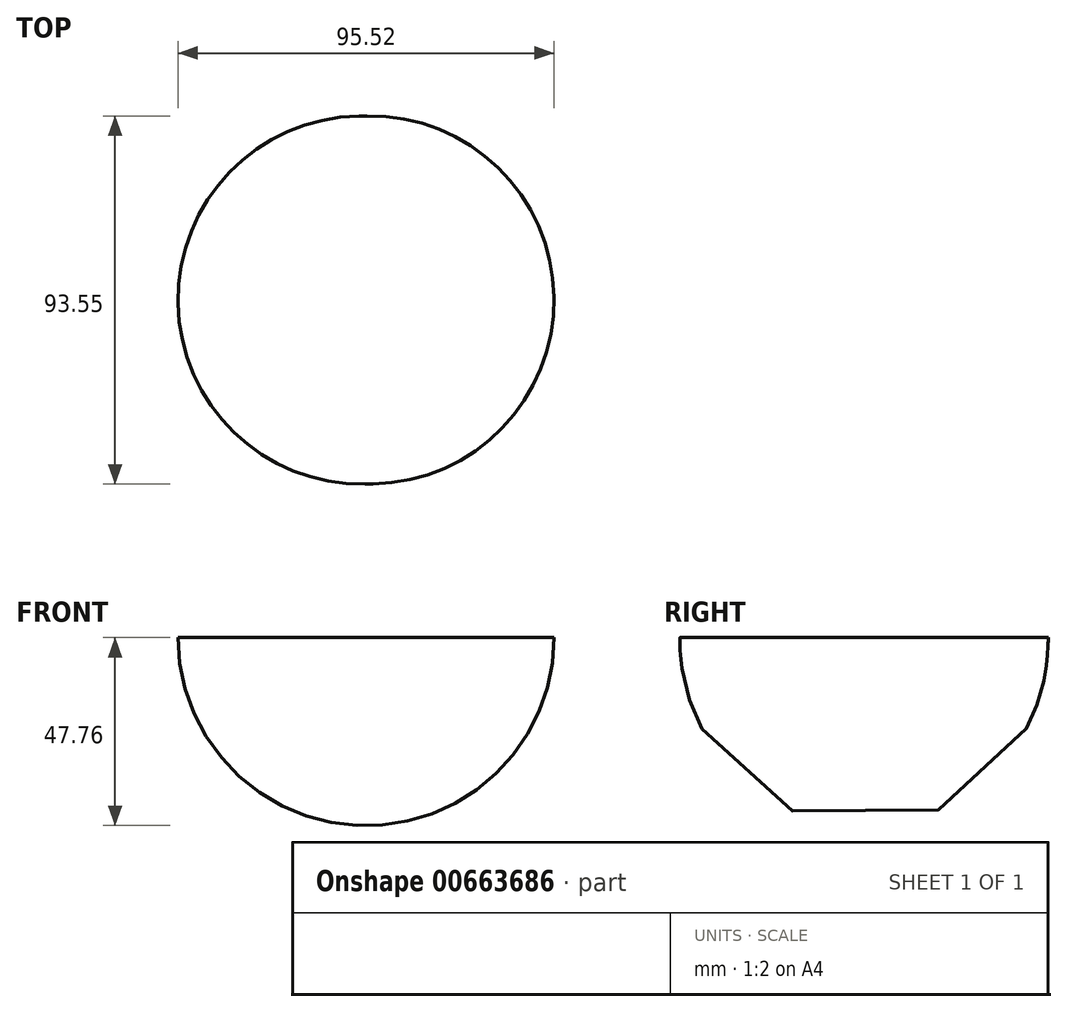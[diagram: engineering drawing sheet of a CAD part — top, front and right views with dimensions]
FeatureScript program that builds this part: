
annotation { "Feature Type Name" : "Feature", "Feature Type Description" : "" }
export const myFeature = defineFeature(function(context is Context, id is Id, definition is map)
    precondition{}
    {
        {
            var Q0;
            Q0=qCreatedBy(makeId("Top.planeOp"),FACE);
            var sketch = newSketch(context, id + "F0", { "sketchPlane" : qUnion([Q0])});
            skCircle(sketch, "E0", {"center": v(0, 0) * mm, "radius": 47 * mm});
            skSolve(sketch);
        }
        {
            var Q0;
            Q0=sQuery(id+"F0.wireOp",EDGE,"E0");
            extrude(context, id + "F1", {"bodyType" : ToolBodyType.SURFACE, "surfaceEntities" : qUnion([Q0]), "depth" : 25.4 * mm, "offsetDistance" : 25.4 * mm});
        }
        {
            var Q0;
            Q0=makeQuery(id+"F0.imprint","IMPRINT",FACE,{"disambiguationData":[TD([[makeQuery(id+"F0.imprint","IMPRINT",EDGE,{"derivedFrom":sQuery(id+"F0.wireOp",EDGE,"E0")}),1.0]])]});
            var sketch = newSketch(context, id + "F2", { "sketchPlane" : qUnion([Q0])});
            skLineSegment(sketch, "E1", {"start": v(0, 46.07) * mm, "end": v(1.53, -47.41) * mm});
            skArc(sketch, "E2", {"start": v(0, 46.07) * mm, "mid": v(-47, -1.45) * mm, "end": v(1.53, -47.41) * mm});
            skSolve(sketch);
        }
        {
            var Q0;
            Q0 = qSketchRegion(id + "F2", true);
            var Q1;
            Q1=sQuery(id+"F2.wireOp",EDGE,"E1");
            revolve(context, id + "F3", {"entities" : qUnion([Q0]), "axis" : qUnion([Q1]), "revolveType" : RevolveType.ONE_DIRECTION, "angle" : 180 * degree});
        }
    });
